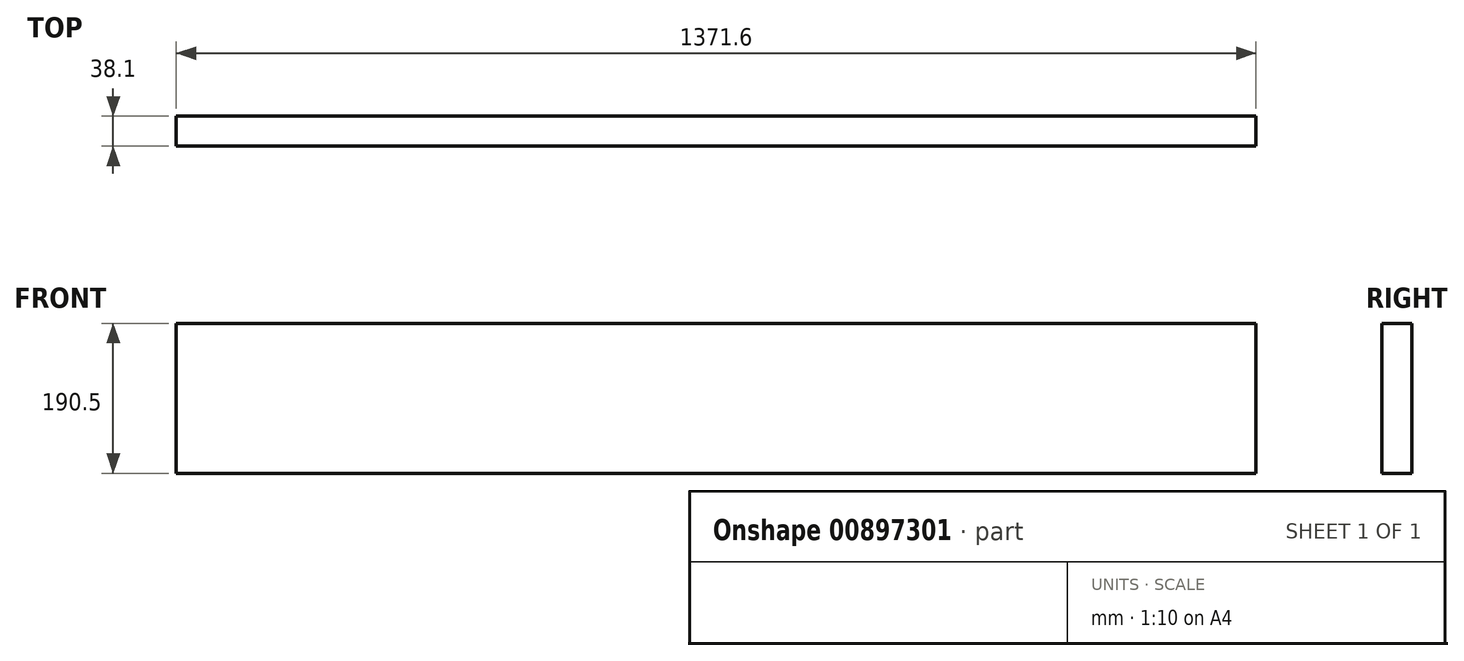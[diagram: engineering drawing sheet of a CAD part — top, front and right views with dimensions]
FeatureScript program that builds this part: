
annotation { "Feature Type Name" : "Feature", "Feature Type Description" : "" }
export const myFeature = defineFeature(function(context is Context, id is Id, definition is map)
    precondition{}
    {
        {
            var Q0;
            Q0=qCreatedBy(makeId("Front.planeOp"),FACE);
            var sketch = newSketch(context, id + "F0", { "sketchPlane" : qUnion([Q0])});
            skLineSegment(sketch, "E0.bottom", {"start": v(-1321.86, 167.11) * mm, "end": v(49.74, 167.11) * mm});
            skLineSegment(sketch, "E0.top", {"start": v(-1321.86, -23.39) * mm, "end": v(49.74, -23.39) * mm});
            skLineSegment(sketch, "E0.left", {"start": v(-1321.86, 167.11) * mm, "end": v(-1321.86, -23.39) * mm});
            skLineSegment(sketch, "E0.right", {"start": v(49.74, 167.11) * mm, "end": v(49.74, -23.39) * mm});
            skSolve(sketch);
        }
        {
            var Q0;
            Q0=makeQuery(id+"F0.imprint","IMPRINT",FACE,{"disambiguationData":[TD([[makeQuery(id+"F0.imprint","IMPRINT",EDGE,{"derivedFrom":sQuery(id+"F0.wireOp",EDGE,"E0.bottom")}),-1.0]])]});
            extrude(context, id + "F1", {"entities" : qUnion([Q0]), "depth" : 38.1 * mm, "offsetDistance" : 25.4 * mm});
        }
    });
